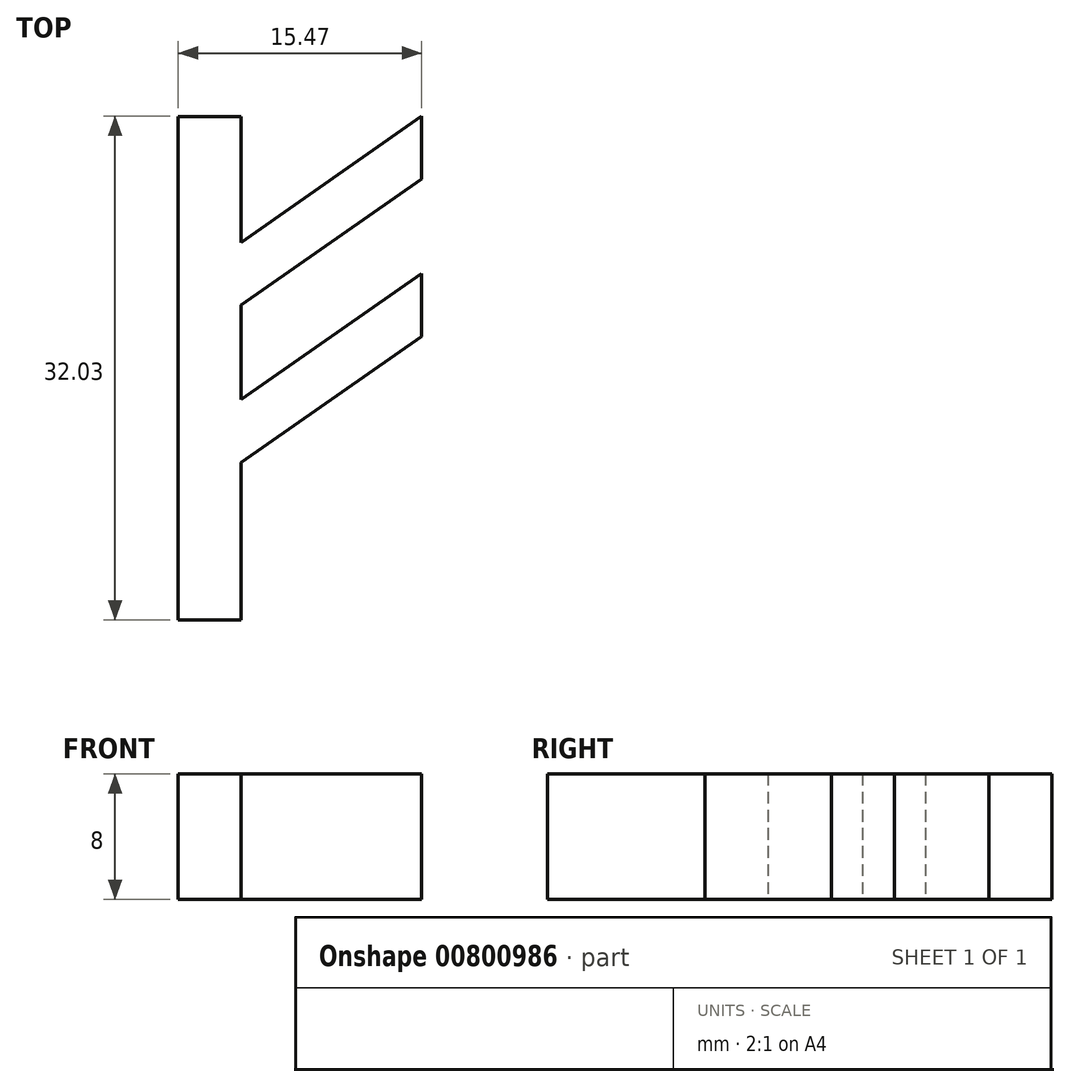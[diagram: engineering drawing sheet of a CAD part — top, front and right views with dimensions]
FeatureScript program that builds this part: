
annotation { "Feature Type Name" : "Feature", "Feature Type Description" : "" }
export const myFeature = defineFeature(function(context is Context, id is Id, definition is map)
    precondition{}
    {
        {
            var Q0;
            Q0=qCreatedBy(makeId("Top.planeOp"),FACE);
            var sketch = newSketch(context, id + "F0", { "sketchPlane" : qUnion([Q0])});
            skLineSegment(sketch, "E0", {"start": v(0, 0) * mm, "end": v(0, -32) * mm});
            skLineSegment(sketch, "E1", {"start": v(0, -32) * mm, "end": v(4, -32) * mm});
            skLineSegment(sketch, "E2", {"start": v(4, -32) * mm, "end": v(4, -22) * mm});
            skLineSegment(sketch, "E3", {"start": v(4, -22) * mm, "end": v(15.47, -13.97) * mm});
            skLineSegment(sketch, "E4", {"start": v(15.47, -13.97) * mm, "end": v(15.47, -9.97) * mm});
            skLineSegment(sketch, "E5", {"start": v(15.47, -9.97) * mm, "end": v(4, -18) * mm});
            skLineSegment(sketch, "E6", {"start": v(4, -18) * mm, "end": v(4, -12) * mm});
            skLineSegment(sketch, "E7", {"start": v(4, -12) * mm, "end": v(15.47, -3.97) * mm});
            skLineSegment(sketch, "E8", {"start": v(4, -8) * mm, "end": v(4, 0) * mm});
            skLineSegment(sketch, "E9", {"start": v(4, 0) * mm, "end": v(0, 0) * mm});
            skLineSegment(sketch, "E10", {"start": v(15.47, -3.97) * mm, "end": v(15.47, 0.03) * mm});
            skLineSegment(sketch, "E11", {"start": v(15.47, 0.03) * mm, "end": v(4, -8) * mm});
            skSolve(sketch);
        }
        {
            var Q0;
            Q0=makeQuery(id+"F0.imprint","IMPRINT",FACE,{"disambiguationData":[TD([[makeQuery(id+"F0.imprint","IMPRINT",EDGE,{"derivedFrom":sQuery(id+"F0.wireOp",EDGE,"E0")}),1.0]])]});
            extrude(context, id + "F1", {"entities" : qUnion([Q0]), "depth" : 8 * mm, "offsetDistance" : 25 * mm});
        }
    });
